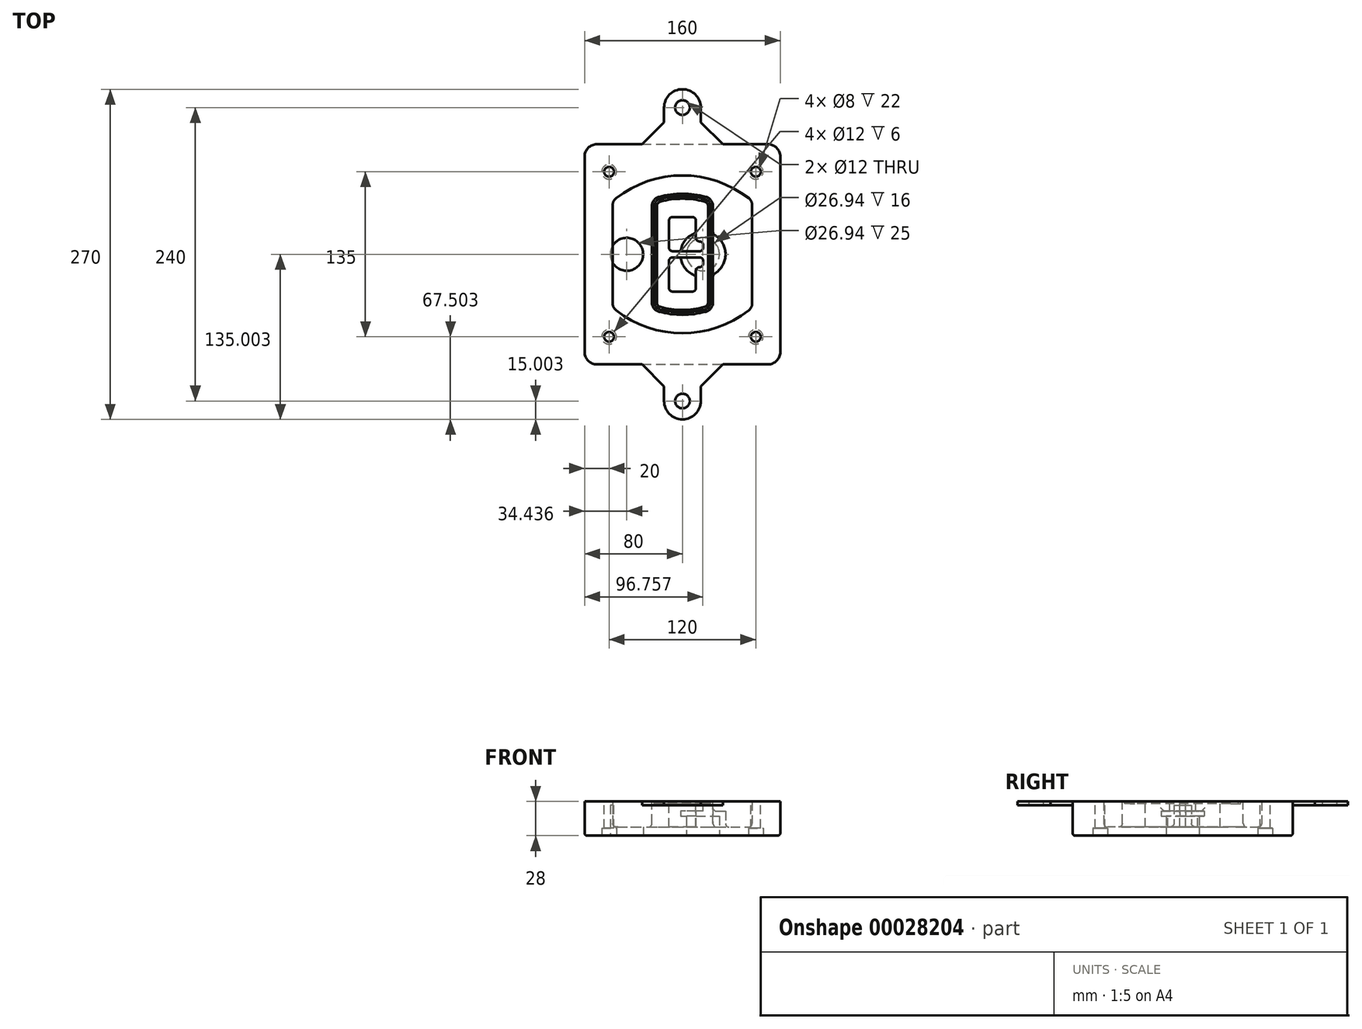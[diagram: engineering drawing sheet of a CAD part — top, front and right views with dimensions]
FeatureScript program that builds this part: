
annotation { "Feature Type Name" : "Feature", "Feature Type Description" : "" }
export const myFeature = defineFeature(function(context is Context, id is Id, definition is map)
    precondition{}
    {
        {
            var Q0;
            Q0=qCreatedBy(makeId("Top.planeOp"),FACE);
            var sketch = newSketch(context, id + "F0", { "sketchPlane" : qUnion([Q0])});
            skPoint(sketch, "E0.rect.middle", {"position": v(0, 0) * mm});
            skLineSegment(sketch, "E1.bottom", {"start": v(24.05, 28.38) * mm, "end": v(164.05, 28.38) * mm});
            skLineSegment(sketch, "E1.top", {"start": v(24.05, 208.38) * mm, "end": v(164.05, 208.38) * mm});
            skLineSegment(sketch, "E1.left", {"start": v(14.05, 38.38) * mm, "end": v(14.05, 198.38) * mm});
            skLineSegment(sketch, "E1.right", {"start": v(174.05, 38.38) * mm, "end": v(174.05, 198.38) * mm});
            skLineSegment(sketch, "E2", {"start": v(14.05, 208.38) * mm, "end": v(174.05, 28.38) * mm, "construction": true});
            skLineSegment(sketch, "E3", {"start": v(174.05, 208.38) * mm, "end": v(14.05, 28.38) * mm, "construction": true});
            skCircle(sketch, "E4", {"center": v(34.05, 185.88) * mm, "radius": 4 * mm});
            skCircle(sketch, "E5", {"center": v(154.05, 185.88) * mm, "radius": 4 * mm});
            skCircle(sketch, "E6", {"center": v(154.05, 50.88) * mm, "radius": 4 * mm});
            skCircle(sketch, "E7", {"center": v(34.05, 50.88) * mm, "radius": 4 * mm});
            skLineSegment(sketch, "E8", {"start": v(34.05, 185.88) * mm, "end": v(154.05, 185.88) * mm, "construction": true});
            skLineSegment(sketch, "E9", {"start": v(154.05, 185.88) * mm, "end": v(154.05, 50.88) * mm, "construction": true});
            skLineSegment(sketch, "E10", {"start": v(154.05, 50.88) * mm, "end": v(34.05, 50.88) * mm, "construction": true});
            skLineSegment(sketch, "E11", {"start": v(34.05, 50.88) * mm, "end": v(34.05, 185.88) * mm, "construction": true});
            skLineSegment(sketch, "E12", {"start": v(34.05, 158.68) * mm, "end": v(34.05, 78.09) * mm});
            skLineSegment(sketch, "E13", {"start": v(154.05, 158.68) * mm, "end": v(154.05, 78.09) * mm});
            skArc(sketch, "E14", {"start": v(150.2, 166.56) * mm, "mid": v(94.05, 185.88) * mm, "end": v(37.9, 166.56) * mm});
            skArc(sketch, "E15", {"start": v(37.9, 70.2) * mm, "mid": v(94.05, 50.88) * mm, "end": v(150.2, 70.2) * mm});
            skLineSegment(sketch, "E16", {"start": v(34.05, 118.38) * mm, "end": v(154.05, 118.38) * mm, "construction": true});
            skPoint(sketch, "E17.visualSharp", {"position": v(34.05, 73.38) * mm});
            skArc(sketch, "E17.filletArc", {"start": v(34.05, 78.09) * mm, "mid": v(35.06, 73.7) * mm, "end": v(37.9, 70.2) * mm});
            skPoint(sketch, "E18.visualSharp", {"position": v(34.05, 163.38) * mm});
            skArc(sketch, "E18.filletArc", {"start": v(37.9, 166.56) * mm, "mid": v(35.06, 163.06) * mm, "end": v(34.05, 158.68) * mm});
            skPoint(sketch, "E19.visualSharp", {"position": v(154.05, 163.38) * mm});
            skArc(sketch, "E19.filletArc", {"start": v(154.05, 158.68) * mm, "mid": v(153.04, 163.06) * mm, "end": v(150.2, 166.56) * mm});
            skPoint(sketch, "E20.visualSharp", {"position": v(154.05, 73.38) * mm});
            skArc(sketch, "E20.filletArc", {"start": v(150.2, 70.2) * mm, "mid": v(153.04, 73.7) * mm, "end": v(154.05, 78.09) * mm});
            skPoint(sketch, "E21.visualSharp", {"position": v(14.05, 208.38) * mm});
            skArc(sketch, "E21.filletArc", {"start": v(24.05, 208.38) * mm, "mid": v(16.98, 205.45) * mm, "end": v(14.05, 198.38) * mm});
            skPoint(sketch, "E22.visualSharp", {"position": v(174.05, 208.38) * mm});
            skArc(sketch, "E22.filletArc", {"start": v(174.05, 198.38) * mm, "mid": v(171.12, 205.45) * mm, "end": v(164.05, 208.38) * mm});
            skPoint(sketch, "E23.visualSharp", {"position": v(174.05, 28.38) * mm});
            skArc(sketch, "E23.filletArc", {"start": v(164.05, 28.38) * mm, "mid": v(171.12, 31.31) * mm, "end": v(174.05, 38.38) * mm});
            skPoint(sketch, "E24.visualSharp", {"position": v(14.05, 28.38) * mm});
            skArc(sketch, "E24.filletArc", {"start": v(14.05, 38.38) * mm, "mid": v(16.98, 31.31) * mm, "end": v(24.05, 28.38) * mm});
            skArc(sketch, "E25.0", {"start": v(151.05, 158.68) * mm, "mid": v(150.34, 161.75) * mm, "end": v(148.36, 164.2) * mm});
            skLineSegment(sketch, "E25.1", {"start": v(151.05, 158.68) * mm, "end": v(151.05, 78.09) * mm});
            skArc(sketch, "E25.2", {"start": v(148.36, 72.57) * mm, "mid": v(150.34, 75.02) * mm, "end": v(151.05, 78.09) * mm});
            skArc(sketch, "E25.3", {"start": v(39.74, 72.57) * mm, "mid": v(94.05, 53.88) * mm, "end": v(148.36, 72.57) * mm});
            skArc(sketch, "E25.4", {"start": v(37.05, 78.09) * mm, "mid": v(37.76, 75.02) * mm, "end": v(39.74, 72.57) * mm});
            skArc(sketch, "E25.5", {"start": v(148.36, 164.2) * mm, "mid": v(94.05, 182.88) * mm, "end": v(39.74, 164.2) * mm});
            skLineSegment(sketch, "E25.6", {"start": v(37.05, 158.68) * mm, "end": v(37.05, 78.09) * mm});
            skArc(sketch, "E25.7", {"start": v(39.74, 164.2) * mm, "mid": v(37.76, 161.75) * mm, "end": v(37.05, 158.68) * mm});
            skArc(sketch, "E26.0", {"start": v(35.43, 169.71) * mm, "mid": v(31.47, 164.82) * mm, "end": v(30.05, 158.68) * mm});
            skArc(sketch, "E26.1", {"start": v(152.67, 169.71) * mm, "mid": v(94.05, 189.88) * mm, "end": v(35.43, 169.71) * mm});
            skArc(sketch, "E26.2", {"start": v(158.05, 158.68) * mm, "mid": v(156.63, 164.82) * mm, "end": v(152.67, 169.71) * mm});
            skLineSegment(sketch, "E26.3", {"start": v(158.05, 158.68) * mm, "end": v(158.05, 78.09) * mm});
            skArc(sketch, "E26.4", {"start": v(152.67, 67.05) * mm, "mid": v(156.63, 71.95) * mm, "end": v(158.05, 78.09) * mm});
            skLineSegment(sketch, "E26.5", {"start": v(30.05, 158.68) * mm, "end": v(30.05, 78.09) * mm});
            skArc(sketch, "E26.6", {"start": v(35.43, 67.05) * mm, "mid": v(94.05, 46.88) * mm, "end": v(152.67, 67.05) * mm});
            skArc(sketch, "E26.7", {"start": v(30.05, 78.09) * mm, "mid": v(31.47, 71.95) * mm, "end": v(35.43, 67.05) * mm});
            skSolve(sketch);
        }
        {
            var Q0;
            Q0=makeQuery(id+"F0.imprint","IMPRINT",FACE,{"disambiguationData":[TD([[makeQuery(id+"F0.imprint","IMPRINT",EDGE,{"derivedFrom":sQuery(id+"F0.wireOp",EDGE,"E1.bottom")}),1.0]])]});
            var Q1;
            Q1=makeQuery(id+"F0.imprint","IMPRINT",FACE,{"disambiguationData":[TD([[makeQuery(id+"F0.imprint","IMPRINT",EDGE,{"derivedFrom":sQuery(id+"F0.wireOp",EDGE,"E12")}),1.0]])]});
            var Q2;
            Q2=makeQuery(id+"F0.imprint","IMPRINT",FACE,{"disambiguationData":[TD([[makeQuery(id+"F0.imprint","IMPRINT",EDGE,{"derivedFrom":sQuery(id+"F0.wireOp",EDGE,"E25.0")}),1.0]])]});
            var Q3;
            Q3=makeQuery(id+"F0.imprint","IMPRINT",FACE,{"disambiguationData":[TD([[makeQuery(id+"F0.imprint","IMPRINT",EDGE,{"derivedFrom":sQuery(id+"F0.wireOp",EDGE,"E12")}),-1.0]])]});
            extrude(context, id + "F1", {"entities" : qUnion([Q0, Q1, Q2, Q3]), "oppositeDirection" : true, "depth" : 25 * mm});
        }
        {
            var Q0;
            Q0=makeQuery(id+"F0.imprint","IMPRINT",FACE,{"disambiguationData":[TD([[makeQuery(id+"F0.imprint","IMPRINT",EDGE,{"derivedFrom":sQuery(id+"F0.wireOp",EDGE,"E12")}),1.0]])]});
            extrude(context, id + "F2", {"entities" : qUnion([Q0]), "operationType" : NewBodyOperationType.ADD, "depth" : 3 * mm});
        }
        {
            var Q0;
            Q0=makeQuery(id+"F0.imprint","IMPRINT",FACE,{"disambiguationData":[TD([[makeQuery(id+"F0.imprint","IMPRINT",EDGE,{"derivedFrom":sQuery(id+"F0.wireOp",EDGE,"E25.0")}),1.0]])]});
            extrude(context, id + "F3", {"entities" : qUnion([Q0]), "operationType" : NewBodyOperationType.REMOVE, "oppositeDirection" : true, "depth" : 18 * mm});
        }
        {
            var Q0;
            Q0=makeQuery(id+"F2.opExtrude","CAP_FACE",FACE,{"disambiguationData":[OSD([sQuery(id+"F0.wireOp",EDGE,"E12"),sQuery(id+"F0.wireOp",EDGE,"E13"),sQuery(id+"F0.wireOp",EDGE,"E14"),sQuery(id+"F0.wireOp",EDGE,"E15"),sQuery(id+"F0.wireOp",EDGE,"E17.filletArc"),sQuery(id+"F0.wireOp",EDGE,"E18.filletArc"),sQuery(id+"F0.wireOp",EDGE,"E19.filletArc"),sQuery(id+"F0.wireOp",EDGE,"E20.filletArc"),sQuery(id+"F0.wireOp",EDGE,"E25.0"),sQuery(id+"F0.wireOp",EDGE,"E25.1"),sQuery(id+"F0.wireOp",EDGE,"E25.2"),sQuery(id+"F0.wireOp",EDGE,"E25.3"),sQuery(id+"F0.wireOp",EDGE,"E25.4"),sQuery(id+"F0.wireOp",EDGE,"E25.5"),sQuery(id+"F0.wireOp",EDGE,"E25.6"),sQuery(id+"F0.wireOp",EDGE,"E25.7")])],"isStart":false});
            var sketch = newSketch(context, id + "F4", { "sketchPlane" : qUnion([Q0])});
            skArc(sketch, "E27.0", {"start": v(74.97, 71.41) * mm, "mid": v(94.05, 68.88) * mm, "end": v(113.13, 71.41) * mm});
            skArc(sketch, "E28.0", {"start": v(113.13, 165.35) * mm, "mid": v(94.05, 167.88) * mm, "end": v(74.97, 165.35) * mm});
            skLineSegment(sketch, "E29", {"start": v(69.05, 157.63) * mm, "end": v(69.05, 79.14) * mm});
            skLineSegment(sketch, "E30", {"start": v(119.05, 157.63) * mm, "end": v(119.05, 79.14) * mm});
            skLineSegment(sketch, "E31", {"start": v(69.05, 163.48) * mm, "end": v(119.05, 163.48) * mm, "construction": true});
            skLineSegment(sketch, "E32", {"start": v(69.05, 73.28) * mm, "end": v(119.05, 73.28) * mm, "construction": true});
            skPoint(sketch, "E33.visualSharp", {"position": v(69.05, 163.48) * mm});
            skArc(sketch, "E33.filletArc", {"start": v(74.97, 165.35) * mm, "mid": v(70.7, 162.5) * mm, "end": v(69.05, 157.63) * mm});
            skPoint(sketch, "E34.visualSharp", {"position": v(119.05, 163.48) * mm});
            skArc(sketch, "E34.filletArc", {"start": v(119.05, 157.63) * mm, "mid": v(117.4, 162.5) * mm, "end": v(113.13, 165.35) * mm});
            skPoint(sketch, "E35.visualSharp", {"position": v(119.05, 73.28) * mm});
            skArc(sketch, "E35.filletArc", {"start": v(113.13, 71.41) * mm, "mid": v(117.4, 74.27) * mm, "end": v(119.05, 79.14) * mm});
            skPoint(sketch, "E36.visualSharp", {"position": v(69.05, 73.28) * mm});
            skArc(sketch, "E36.filletArc", {"start": v(69.05, 79.14) * mm, "mid": v(70.7, 74.27) * mm, "end": v(74.97, 71.41) * mm});
            skArc(sketch, "E37.0", {"start": v(148.36, 164.2) * mm, "mid": v(94.05, 182.88) * mm, "end": v(39.74, 164.2) * mm});
            skArc(sketch, "E37.1", {"start": v(39.74, 164.2) * mm, "mid": v(37.76, 161.75) * mm, "end": v(37.05, 158.68) * mm});
            skLineSegment(sketch, "E37.2", {"start": v(37.05, 158.68) * mm, "end": v(37.05, 78.09) * mm});
            skArc(sketch, "E37.3", {"start": v(37.05, 78.09) * mm, "mid": v(37.76, 75.02) * mm, "end": v(39.74, 72.57) * mm});
            skArc(sketch, "E37.4", {"start": v(39.74, 72.57) * mm, "mid": v(94.05, 53.88) * mm, "end": v(148.36, 72.57) * mm});
            skArc(sketch, "E37.5", {"start": v(148.36, 72.57) * mm, "mid": v(150.34, 75.02) * mm, "end": v(151.05, 78.09) * mm});
            skLineSegment(sketch, "E37.6", {"start": v(151.05, 158.68) * mm, "end": v(151.05, 78.09) * mm});
            skArc(sketch, "E37.7", {"start": v(151.05, 158.68) * mm, "mid": v(150.34, 161.75) * mm, "end": v(148.36, 164.2) * mm});
            skLineSegment(sketch, "E38.0", {"start": v(117.05, 157.63) * mm, "end": v(117.05, 79.14) * mm});
            skArc(sketch, "E38.1", {"start": v(112.61, 73.34) * mm, "mid": v(115.81, 75.49) * mm, "end": v(117.05, 79.14) * mm});
            skArc(sketch, "E38.2", {"start": v(75.49, 73.34) * mm, "mid": v(94.05, 70.88) * mm, "end": v(112.61, 73.34) * mm});
            skArc(sketch, "E38.3", {"start": v(71.05, 79.14) * mm, "mid": v(72.29, 75.49) * mm, "end": v(75.49, 73.34) * mm});
            skLineSegment(sketch, "E38.4", {"start": v(71.05, 157.63) * mm, "end": v(71.05, 79.14) * mm});
            skArc(sketch, "E38.5", {"start": v(117.05, 157.63) * mm, "mid": v(115.81, 161.28) * mm, "end": v(112.61, 163.42) * mm});
            skArc(sketch, "E38.6", {"start": v(75.49, 163.42) * mm, "mid": v(72.29, 161.28) * mm, "end": v(71.05, 157.63) * mm});
            skArc(sketch, "E38.7", {"start": v(112.61, 163.42) * mm, "mid": v(94.05, 165.88) * mm, "end": v(75.49, 163.42) * mm});
            skArc(sketch, "E39.0", {"start": v(115.05, 157.63) * mm, "mid": v(114.23, 160.06) * mm, "end": v(112.1, 161.5) * mm});
            skLineSegment(sketch, "E39.1", {"start": v(115.05, 157.63) * mm, "end": v(115.05, 79.14) * mm});
            skArc(sketch, "E39.2", {"start": v(112.1, 75.27) * mm, "mid": v(114.23, 76.7) * mm, "end": v(115.05, 79.14) * mm});
            skArc(sketch, "E39.3", {"start": v(76, 75.27) * mm, "mid": v(94.05, 72.88) * mm, "end": v(112.1, 75.27) * mm});
            skArc(sketch, "E39.4", {"start": v(73.05, 79.14) * mm, "mid": v(73.87, 76.7) * mm, "end": v(76, 75.27) * mm});
            skArc(sketch, "E39.5", {"start": v(112.1, 161.5) * mm, "mid": v(94.05, 163.88) * mm, "end": v(76, 161.5) * mm});
            skLineSegment(sketch, "E39.6", {"start": v(73.05, 157.63) * mm, "end": v(73.05, 79.14) * mm});
            skArc(sketch, "E39.7", {"start": v(76, 161.5) * mm, "mid": v(73.87, 160.06) * mm, "end": v(73.05, 157.63) * mm});
            skLineSegment(sketch, "E40", {"start": v(69.05, 118.38) * mm, "end": v(119.05, 118.38) * mm, "construction": true});
            skLineSegment(sketch, "E41", {"start": v(83.05, 123.88) * mm, "end": v(83.05, 145.88) * mm});
            skLineSegment(sketch, "E42", {"start": v(86.05, 148.88) * mm, "end": v(102.05, 148.88) * mm});
            skLineSegment(sketch, "E43", {"start": v(105.05, 145.88) * mm, "end": v(105.05, 131.88) * mm});
            skLineSegment(sketch, "E44", {"start": v(108.05, 128.88) * mm, "end": v(108.05, 128.88) * mm});
            skLineSegment(sketch, "E45", {"start": v(111.05, 125.88) * mm, "end": v(111.05, 123.88) * mm});
            skLineSegment(sketch, "E46", {"start": v(108.05, 120.88) * mm, "end": v(86.05, 120.88) * mm});
            skPoint(sketch, "E47.visualSharp", {"position": v(83.05, 148.88) * mm});
            skArc(sketch, "E47.filletArc", {"start": v(86.05, 148.88) * mm, "mid": v(83.93, 148) * mm, "end": v(83.05, 145.88) * mm});
            skPoint(sketch, "E48.visualSharp", {"position": v(105.05, 148.88) * mm});
            skArc(sketch, "E48.filletArc", {"start": v(105.05, 145.88) * mm, "mid": v(104.17, 148) * mm, "end": v(102.05, 148.88) * mm});
            skPoint(sketch, "E49.visualSharp", {"position": v(105.05, 128.88) * mm});
            skArc(sketch, "E49.filletArc", {"start": v(105.05, 131.88) * mm, "mid": v(105.93, 129.76) * mm, "end": v(108.05, 128.88) * mm});
            skPoint(sketch, "E50.visualSharp", {"position": v(111.05, 128.88) * mm});
            skArc(sketch, "E50.filletArc", {"start": v(111.05, 125.88) * mm, "mid": v(110.17, 128) * mm, "end": v(108.05, 128.88) * mm});
            skPoint(sketch, "E51.visualSharp", {"position": v(111.05, 120.88) * mm});
            skArc(sketch, "E51.filletArc", {"start": v(108.05, 120.88) * mm, "mid": v(110.17, 121.76) * mm, "end": v(111.05, 123.88) * mm});
            skPoint(sketch, "E52.visualSharp", {"position": v(83.05, 120.88) * mm});
            skArc(sketch, "E52.filletArc", {"start": v(83.05, 123.88) * mm, "mid": v(83.93, 121.76) * mm, "end": v(86.05, 120.88) * mm});
            skLineSegment(sketch, "E53.0.MirrorCS", {"start": v(108.05, 115.88) * mm, "end": v(86.05, 115.88) * mm});
            skArc(sketch, "E54.0.MirrorCS", {"start": v(83.05, 112.88) * mm, "mid": v(83.93, 115) * mm, "end": v(86.05, 115.88) * mm});
            skLineSegment(sketch, "E55.0.MirrorCS", {"start": v(83.05, 112.88) * mm, "end": v(83.05, 90.88) * mm});
            skArc(sketch, "E56.0.MirrorCS", {"start": v(86.05, 87.88) * mm, "mid": v(83.93, 88.76) * mm, "end": v(83.05, 90.88) * mm});
            skLineSegment(sketch, "E57.0.MirrorCS", {"start": v(86.05, 87.88) * mm, "end": v(102.05, 87.88) * mm});
            skArc(sketch, "E58.0.MirrorCS", {"start": v(105.05, 90.88) * mm, "mid": v(104.17, 88.76) * mm, "end": v(102.05, 87.88) * mm});
            skLineSegment(sketch, "E59.0.MirrorCS", {"start": v(105.05, 90.88) * mm, "end": v(105.05, 104.88) * mm});
            skArc(sketch, "E60.0.MirrorCS", {"start": v(105.05, 104.88) * mm, "mid": v(105.93, 107) * mm, "end": v(108.05, 107.88) * mm});
            skArc(sketch, "E61.0.MirrorCS", {"start": v(111.05, 110.88) * mm, "mid": v(110.17, 108.76) * mm, "end": v(108.05, 107.88) * mm});
            skLineSegment(sketch, "E62.0.MirrorCS", {"start": v(111.05, 110.88) * mm, "end": v(111.05, 112.88) * mm});
            skArc(sketch, "E63.0.MirrorCS", {"start": v(108.05, 115.88) * mm, "mid": v(110.17, 115) * mm, "end": v(111.05, 112.88) * mm});
            skSolve(sketch);
        }
        {
            var Q0;
            Q0=makeQuery(id+"F4.imprint","IMPRINT",FACE,{"disambiguationData":[TD([[makeQuery(id+"F4.imprint","IMPRINT",EDGE,{"derivedFrom":sQuery(id+"F4.wireOp",EDGE,"E27.0")}),1.0]])]});
            var Q1;
            Q1=makeQuery(id+"F4.imprint","IMPRINT",FACE,{"disambiguationData":[TD([[makeQuery(id+"F4.imprint","IMPRINT",EDGE,{"derivedFrom":sQuery(id+"F4.wireOp",EDGE,"E38.0")}),-1.0]])]});
            var Q2;
            Q2=makeQuery(id+"F4.imprint","IMPRINT",FACE,{"disambiguationData":[TD([[makeQuery(id+"F4.imprint","IMPRINT",EDGE,{"derivedFrom":sQuery(id+"F4.wireOp",EDGE,"E39.0")}),1.0]])]});
            extrude(context, id + "F5", {"entities" : qUnion([Q0, Q1, Q2]), "operationType" : NewBodyOperationType.ADD, "endBound" : BoundingType.UP_TO_NEXT, "oppositeDirection" : true, "depth" : 25 * mm});
        }
        {
            var Q0;
            Q0=makeQuery(id+"F4.imprint","IMPRINT",FACE,{"disambiguationData":[TD([[makeQuery(id+"F4.imprint","IMPRINT",EDGE,{"derivedFrom":sQuery(id+"F4.wireOp",EDGE,"E38.0")}),-1.0]])]});
            extrude(context, id + "F6", {"entities" : qUnion([Q0]), "operationType" : NewBodyOperationType.REMOVE, "oppositeDirection" : true, "depth" : 2 * mm});
        }
        {
            var Q0;
            Q0=makeQuery(id+"F1.opExtrude","CAP_FACE",FACE,{"disambiguationData":[OSD([sQuery(id+"F0.wireOp",EDGE,"E1.bottom"),sQuery(id+"F0.wireOp",EDGE,"E1.top"),sQuery(id+"F0.wireOp",EDGE,"E1.left"),sQuery(id+"F0.wireOp",EDGE,"E1.right"),sQuery(id+"F0.wireOp",EDGE,"E4"),sQuery(id+"F0.wireOp",EDGE,"E5"),sQuery(id+"F0.wireOp",EDGE,"E6"),sQuery(id+"F0.wireOp",EDGE,"E7"),sQuery(id+"F0.wireOp",EDGE,"E21.filletArc"),sQuery(id+"F0.wireOp",EDGE,"E22.filletArc"),sQuery(id+"F0.wireOp",EDGE,"E23.filletArc"),sQuery(id+"F0.wireOp",EDGE,"E24.filletArc")])],"isStart":false});
            var sketch = newSketch(context, id + "F7", { "sketchPlane" : qUnion([Q0])});
            skCircle(sketch, "E64", {"center": v(110.8, -118.38) * mm, "radius": 13.47 * mm});
            skCircle(sketch, "E65", {"center": v(48.49, -118.38) * mm, "radius": 13.47 * mm});
            skLineSegment(sketch, "E66", {"start": v(174.05, -118.38) * mm, "end": v(14.05, -118.38) * mm});
            skCircle(sketch, "E67", {"center": v(110.8, -118.38) * mm, "radius": 18.47 * mm});
            skCircle(sketch, "E68", {"center": v(154.05, -185.88) * mm, "radius": 6 * mm});
            skCircle(sketch, "E69", {"center": v(34.05, -185.88) * mm, "radius": 6 * mm});
            skCircle(sketch, "E70", {"center": v(34.05, -50.88) * mm, "radius": 6 * mm});
            skCircle(sketch, "E71", {"center": v(154.05, -50.88) * mm, "radius": 6 * mm});
            skSolve(sketch);
        }
        {
            var Q0;
            {var subQ1=sQuery(id+"F7.wireOp",EDGE,"E66");var subQ4=sQuery(id+"F7.wireOp",EDGE,"E64");var subQ6=makeQuery(id+"F7.imprint","INTERSECT",VERTEX,{"disambiguationData":[OD(0.0)],"derivedFrom":[subQ4,subQ1]});Q0=makeQuery(id+"F7.imprint","IMPRINT",FACE,{"disambiguationData":[TD([[makeQuery(id+"F7.imprint","IMPRINT",EDGE,{"disambiguationData":[TD([[subQ6,-1.0]])],"derivedFrom":subQ4}),-1.0]])]});}
            var Q1;
            {var subQ0=sQuery(id+"F7.wireOp",EDGE,"E66");var subQ1=sQuery(id+"F7.wireOp",EDGE,"E64");var subQ3=makeQuery(id+"F7.imprint","INTERSECT",VERTEX,{"disambiguationData":[OD(0.0)],"derivedFrom":[subQ1,subQ0]});Q1=makeQuery(id+"F7.imprint","IMPRINT",FACE,{"disambiguationData":[TD([[makeQuery(id+"F7.imprint","IMPRINT",EDGE,{"disambiguationData":[TD([[subQ3,-1.0]])],"derivedFrom":subQ1}),1.0]])]});}
            var Q2;
            {var subQ0=sQuery(id+"F7.wireOp",EDGE,"E66");var subQ1=sQuery(id+"F7.wireOp",EDGE,"E64");var subQ3=makeQuery(id+"F7.imprint","INTERSECT",VERTEX,{"disambiguationData":[OD(0.0)],"derivedFrom":[subQ1,subQ0]});Q2=makeQuery(id+"F7.imprint","IMPRINT",FACE,{"disambiguationData":[TD([[makeQuery(id+"F7.imprint","IMPRINT",EDGE,{"disambiguationData":[TD([[subQ3,1.0]])],"derivedFrom":subQ1}),1.0]])]});}
            var Q3;
            {var subQ1=sQuery(id+"F7.wireOp",EDGE,"E66");var subQ4=sQuery(id+"F7.wireOp",EDGE,"E64");var subQ6=makeQuery(id+"F7.imprint","INTERSECT",VERTEX,{"disambiguationData":[OD(0.0)],"derivedFrom":[subQ4,subQ1]});Q3=makeQuery(id+"F7.imprint","IMPRINT",FACE,{"disambiguationData":[TD([[makeQuery(id+"F7.imprint","IMPRINT",EDGE,{"disambiguationData":[TD([[subQ6,1.0]])],"derivedFrom":subQ4}),-1.0]])]});}
            extrude(context, id + "F8", {"entities" : qUnion([Q0, Q1, Q2, Q3]), "operationType" : NewBodyOperationType.ADD, "oppositeDirection" : true, "depth" : 20 * mm});
        }
        {
            var Q0;
            {var subQ0=sQuery(id+"F7.wireOp",EDGE,"E66");var subQ1=sQuery(id+"F7.wireOp",EDGE,"E64");var subQ3=makeQuery(id+"F7.imprint","INTERSECT",VERTEX,{"disambiguationData":[OD(0.0)],"derivedFrom":[subQ1,subQ0]});Q0=makeQuery(id+"F7.imprint","IMPRINT",FACE,{"disambiguationData":[TD([[makeQuery(id+"F7.imprint","IMPRINT",EDGE,{"disambiguationData":[TD([[subQ3,-1.0]])],"derivedFrom":subQ1}),1.0]])]});}
            var Q1;
            {var subQ0=sQuery(id+"F7.wireOp",EDGE,"E66");var subQ1=sQuery(id+"F7.wireOp",EDGE,"E64");var subQ3=makeQuery(id+"F7.imprint","INTERSECT",VERTEX,{"disambiguationData":[OD(0.0)],"derivedFrom":[subQ1,subQ0]});Q1=makeQuery(id+"F7.imprint","IMPRINT",FACE,{"disambiguationData":[TD([[makeQuery(id+"F7.imprint","IMPRINT",EDGE,{"disambiguationData":[TD([[subQ3,1.0]])],"derivedFrom":subQ1}),1.0]])]});}
            extrude(context, id + "F9", {"entities" : qUnion([Q0, Q1]), "operationType" : NewBodyOperationType.REMOVE, "oppositeDirection" : true, "depth" : 16 * mm});
        }
        {
            var Q0;
            {var subQ0=sQuery(id+"F7.wireOp",EDGE,"E66");var subQ1=sQuery(id+"F7.wireOp",EDGE,"E65");var subQ3=makeQuery(id+"F7.imprint","INTERSECT",VERTEX,{"disambiguationData":[OD(0.0)],"derivedFrom":[subQ1,subQ0]});Q0=makeQuery(id+"F7.imprint","IMPRINT",FACE,{"disambiguationData":[TD([[makeQuery(id+"F7.imprint","IMPRINT",EDGE,{"disambiguationData":[TD([[subQ3,-1.0]])],"derivedFrom":subQ1}),1.0]])]});}
            var Q1;
            {var subQ0=sQuery(id+"F7.wireOp",EDGE,"E66");var subQ1=sQuery(id+"F7.wireOp",EDGE,"E65");var subQ3=makeQuery(id+"F7.imprint","INTERSECT",VERTEX,{"disambiguationData":[OD(0.0)],"derivedFrom":[subQ1,subQ0]});Q1=makeQuery(id+"F7.imprint","IMPRINT",FACE,{"disambiguationData":[TD([[makeQuery(id+"F7.imprint","IMPRINT",EDGE,{"disambiguationData":[TD([[subQ3,1.0]])],"derivedFrom":subQ1}),1.0]])]});}
            extrude(context, id + "F10", {"entities" : qUnion([Q0, Q1]), "operationType" : NewBodyOperationType.REMOVE, "oppositeDirection" : true, "depth" : 25 * mm});
        }
        {
            var Q0;
            Q0=makeQuery(id+"F7.imprint","IMPRINT",FACE,{"disambiguationData":[TD([[makeQuery(id+"F7.imprint","IMPRINT",EDGE,{"derivedFrom":sQuery(id+"F7.wireOp",EDGE,"E68")}),1.0]])]});
            var Q1;
            Q1=makeQuery(id+"F7.imprint","IMPRINT",FACE,{"disambiguationData":[TD([[makeQuery(id+"F7.imprint","IMPRINT",EDGE,{"derivedFrom":makeQuery(id+"F1.opExtrude","CAP_EDGE",EDGE,{"disambiguationData":[OSD([sQuery(id+"F0.wireOp",EDGE,"E5")])],"isStart":false})}),-1.0]])]});
            var Q2;
            Q2=makeQuery(id+"F7.imprint","IMPRINT",FACE,{"disambiguationData":[TD([[makeQuery(id+"F7.imprint","IMPRINT",EDGE,{"derivedFrom":sQuery(id+"F7.wireOp",EDGE,"E69")}),1.0]])]});
            var Q3;
            Q3=makeQuery(id+"F7.imprint","IMPRINT",FACE,{"disambiguationData":[TD([[makeQuery(id+"F7.imprint","IMPRINT",EDGE,{"derivedFrom":makeQuery(id+"F1.opExtrude","CAP_EDGE",EDGE,{"disambiguationData":[OSD([sQuery(id+"F0.wireOp",EDGE,"E4")])],"isStart":false})}),-1.0]])]});
            var Q4;
            Q4=makeQuery(id+"F7.imprint","IMPRINT",FACE,{"disambiguationData":[TD([[makeQuery(id+"F7.imprint","IMPRINT",EDGE,{"derivedFrom":sQuery(id+"F7.wireOp",EDGE,"E70")}),1.0]])]});
            var Q5;
            Q5=makeQuery(id+"F7.imprint","IMPRINT",FACE,{"disambiguationData":[TD([[makeQuery(id+"F7.imprint","IMPRINT",EDGE,{"derivedFrom":makeQuery(id+"F1.opExtrude","CAP_EDGE",EDGE,{"disambiguationData":[OSD([sQuery(id+"F0.wireOp",EDGE,"E7")])],"isStart":false})}),-1.0]])]});
            var Q6;
            Q6=makeQuery(id+"F7.imprint","IMPRINT",FACE,{"disambiguationData":[TD([[makeQuery(id+"F7.imprint","IMPRINT",EDGE,{"derivedFrom":sQuery(id+"F7.wireOp",EDGE,"E71")}),1.0]])]});
            var Q7;
            Q7=makeQuery(id+"F7.imprint","IMPRINT",FACE,{"disambiguationData":[TD([[makeQuery(id+"F7.imprint","IMPRINT",EDGE,{"derivedFrom":makeQuery(id+"F1.opExtrude","CAP_EDGE",EDGE,{"disambiguationData":[OSD([sQuery(id+"F0.wireOp",EDGE,"E6")])],"isStart":false})}),-1.0]])]});
            extrude(context, id + "F11", {"entities" : qUnion([Q0, Q1, Q2, Q3, Q4, Q5, Q6, Q7]), "operationType" : NewBodyOperationType.REMOVE, "oppositeDirection" : true, "depth" : 6 * mm});
        }
        {
            var Q0;
            Q0=makeQuery(id+"F9.boolean.opBoolean","COPY",FACE,{"derivedFrom":makeQuery(id+"F9.opExtrude","CAP_FACE",FACE,{"disambiguationData":[OSD([sQuery(id+"F7.wireOp",EDGE,"E64")])],"isStart":false})});
            var sketch = newSketch(context, id + "F12", { "sketchPlane" : qUnion([Q0])});
            skArc(sketch, "E72.0", {"start": v(105.05, -100.83) * mm, "mid": v(96.62, -106.56) * mm, "end": v(92.5, -115.88) * mm});
            skArc(sketch, "E72.1", {"start": v(92.5, -120.88) * mm, "mid": v(96.62, -130.2) * mm, "end": v(105.05, -135.93) * mm});
            skLineSegment(sketch, "E73", {"start": v(92.5, -120.88) * mm, "end": v(108.05, -120.88) * mm});
            skLineSegment(sketch, "E74.0", {"start": v(108.05, -115.88) * mm, "end": v(92.5, -115.88) * mm});
            skArc(sketch, "E74.1", {"start": v(108.05, -115.88) * mm, "mid": v(110.17, -115) * mm, "end": v(111.05, -112.88) * mm});
            skLineSegment(sketch, "E74.2", {"start": v(111.05, -110.88) * mm, "end": v(111.05, -112.88) * mm});
            skArc(sketch, "E74.3", {"start": v(111.05, -110.88) * mm, "mid": v(110.17, -108.76) * mm, "end": v(108.05, -107.88) * mm});
            skArc(sketch, "E74.4", {"start": v(105.05, -104.88) * mm, "mid": v(105.93, -107) * mm, "end": v(108.05, -107.88) * mm});
            skLineSegment(sketch, "E74.5", {"start": v(105.05, -100.83) * mm, "end": v(105.05, -104.88) * mm});
            skLineSegment(sketch, "E74.7", {"start": v(108.05, -120.88) * mm, "end": v(92.5, -120.88) * mm});
            skArc(sketch, "E74.8", {"start": v(108.05, -120.88) * mm, "mid": v(110.17, -121.76) * mm, "end": v(111.05, -123.88) * mm});
            skLineSegment(sketch, "E74.9", {"start": v(111.05, -125.88) * mm, "end": v(111.05, -123.88) * mm});
            skArc(sketch, "E74.10", {"start": v(111.05, -125.88) * mm, "mid": v(110.17, -128) * mm, "end": v(108.05, -128.88) * mm});
            skArc(sketch, "E74.11", {"start": v(105.05, -131.88) * mm, "mid": v(105.93, -129.76) * mm, "end": v(108.05, -128.88) * mm});
            skLineSegment(sketch, "E74.12", {"start": v(105.05, -135.93) * mm, "end": v(105.05, -131.88) * mm});
            skPoint(sketch, "E75.orphan", {"position": v(105.05, -145.88) * mm});
            skPoint(sketch, "E76.orphan", {"position": v(86.05, -120.88) * mm});
            skPoint(sketch, "E77.orphan", {"position": v(86.05, -115.88) * mm});
            skPoint(sketch, "E78.orphan", {"position": v(105.05, -90.88) * mm});
            skSolve(sketch);
        }
        {
            var Q0;
            {var subQ7=sQuery(id+"F12.wireOp",EDGE,"E72.0");var subQ14=sQuery(id+"F12.wireOp",EDGE,"E72.1");var subQ16=sQuery(id+"F12.wireOp",EDGE,"E74.1");var subQ18=sQuery(id+"F12.wireOp",EDGE,"E74.8");Q0=qUnion([makeQuery(id+"F12.imprint","IMPRINT",FACE,{"disambiguationData":[TD([[makeQuery(id+"F12.imprint","IMPRINT",EDGE,{"derivedFrom":subQ7}),1.0]])]}),makeQuery(id+"F12.imprint","IMPRINT",FACE,{"disambiguationData":[TD([[makeQuery(id+"F12.imprint","IMPRINT",EDGE,{"derivedFrom":subQ14}),1.0]])]}),makeQuery(id+"F12.imprint","IMPRINT",FACE,{"disambiguationData":[TD([[makeQuery(id+"F12.imprint","IMPRINT",EDGE,{"derivedFrom":subQ16}),1.0]])]}),makeQuery(id+"F12.imprint","IMPRINT",FACE,{"disambiguationData":[TD([[makeQuery(id+"F12.imprint","IMPRINT",EDGE,{"derivedFrom":subQ18}),-1.0]])]})]);}
            var Q1;
            Q1=makeQuery(id+"F5.boolean.opBoolean","SPLIT",FACE,{"disambiguationData":[TD([makeQuery(id+"F5.opExtrude","SWEPT_FACE",FACE,{"disambiguationData":[OSD([sQuery(id+"F4.wireOp",EDGE,"E41")])]})])],"derivedFrom":makeQuery(id+"F3.boolean.opBoolean","COPY",FACE,{"derivedFrom":makeQuery(id+"F3.opExtrude","CAP_FACE",FACE,{"disambiguationData":[OSD([sQuery(id+"F0.wireOp",EDGE,"E25.0"),sQuery(id+"F0.wireOp",EDGE,"E25.1"),sQuery(id+"F0.wireOp",EDGE,"E25.2"),sQuery(id+"F0.wireOp",EDGE,"E25.3"),sQuery(id+"F0.wireOp",EDGE,"E25.4"),sQuery(id+"F0.wireOp",EDGE,"E25.5"),sQuery(id+"F0.wireOp",EDGE,"E25.6"),sQuery(id+"F0.wireOp",EDGE,"E25.7")])],"isStart":false})})});
            extrude(context, id + "F13", {"entities" : qUnion([Q0]), "operationType" : NewBodyOperationType.REMOVE, "endBound" : BoundingType.UP_TO_SURFACE, "endBoundEntityFace" : qUnion([Q1]), "depth" : 25 * mm});
        }
        {
            var Q0;
            Q0=makeQuery(id+"F3.boolean.opBoolean","COPY",EDGE,{"derivedFrom":makeQuery(id+"F3.opExtrude","CAP_EDGE",EDGE,{"disambiguationData":[OSD([sQuery(id+"F0.wireOp",EDGE,"E25.6")])],"isStart":false})});
            var Q1;
            Q1=makeQuery(id+"F8.boolean.opBoolean","INTERSECT",EDGE,{"derivedFrom":[makeQuery(id+"F5.opExtrude","SWEPT_FACE",FACE,{"disambiguationData":[OSD([sQuery(id+"F4.wireOp",EDGE,"E30")])]}),makeQuery(id+"F8.opExtrude","CAP_FACE",FACE,{"disambiguationData":[OSD([sQuery(id+"F7.wireOp",EDGE,"E67")])],"isStart":false})]});
            var Q2;
            Q2=makeQuery(id+"F8.boolean.opBoolean","INTERSECT",EDGE,{"disambiguationData":[OD(1.0)],"derivedFrom":[makeQuery(id+"F5.opExtrude","SWEPT_FACE",FACE,{"disambiguationData":[OSD([sQuery(id+"F4.wireOp",EDGE,"E30")])]}),makeQuery(id+"F8.opExtrude","SWEPT_FACE",FACE,{"disambiguationData":[OSD([sQuery(id+"F7.wireOp",EDGE,"E67")])]})]});
            var Q3;
            {var subQ0=sQuery(id+"F4.wireOp",EDGE,"E30");Q3=makeQuery(id+"F8.boolean.opBoolean","SPLIT",EDGE,{"disambiguationData":[TD([makeQuery(id+"F5.opExtrude","SWEPT_FACE",FACE,{"disambiguationData":[OSD([sQuery(id+"F4.wireOp",EDGE,"E35.filletArc")])]})])],"derivedFrom":makeQuery(id+"F5.opExtrude","CAP_EDGE",EDGE,{"disambiguationData":[OSD([subQ0])],"isStart":false})});}
            var Q4;
            {var subQ0=sQuery(id+"F0.wireOp",EDGE,"E25.7");var subQ1=sQuery(id+"F0.wireOp",EDGE,"E25.1");var subQ2=sQuery(id+"F0.wireOp",EDGE,"E25.6");var subQ3=sQuery(id+"F0.wireOp",EDGE,"E25.5");var subQ4=sQuery(id+"F0.wireOp",EDGE,"E25.4");var subQ5=sQuery(id+"F0.wireOp",EDGE,"E25.0");var subQ6=sQuery(id+"F0.wireOp",EDGE,"E25.2");var subQ7=sQuery(id+"F0.wireOp",EDGE,"E25.3");Q4=makeQuery(id+"F8.boolean.opBoolean","INTERSECT",EDGE,{"derivedFrom":[makeQuery(id+"F5.boolean.opBoolean","SPLIT",FACE,{"disambiguationData":[TD([makeQuery(id+"F2.opExtrude","SWEPT_FACE",FACE,{"disambiguationData":[OSD([subQ5])]})])],"derivedFrom":makeQuery(id+"F3.boolean.opBoolean","COPY",FACE,{"derivedFrom":makeQuery(id+"F3.opExtrude","CAP_FACE",FACE,{"disambiguationData":[OSD([subQ5,subQ1,subQ6,subQ7,subQ4,subQ3,subQ2,subQ0])],"isStart":false})})}),makeQuery(id+"F8.opExtrude","SWEPT_FACE",FACE,{"disambiguationData":[OSD([sQuery(id+"F7.wireOp",EDGE,"E67")])]})]});}
            var Q5;
            Q5=makeQuery(id+"F8.boolean.opBoolean","INTERSECT",EDGE,{"disambiguationData":[OD(0.0)],"derivedFrom":[makeQuery(id+"F5.opExtrude","SWEPT_FACE",FACE,{"disambiguationData":[OSD([sQuery(id+"F4.wireOp",EDGE,"E30")])]}),makeQuery(id+"F8.opExtrude","SWEPT_FACE",FACE,{"disambiguationData":[OSD([sQuery(id+"F7.wireOp",EDGE,"E67")])]})]});
            fillet(context, id + "F14", {"entities" : qUnion([Q0, Q1, Q2, Q3, Q4, Q5]), "radius" : 3 * mm, "tangentPropagation" : true, "allowEdgeOverflow" : false});
        }
        {
            var Q0;
            Q0=makeQuery(id+"F1.opExtrude","CAP_EDGE",EDGE,{"disambiguationData":[OSD([sQuery(id+"F0.wireOp",EDGE,"E1.bottom")])],"isStart":false});
            fillet(context, id + "F15", {"entities" : qUnion([Q0]), "radius" : 2 * mm, "tangentPropagation" : true, "allowEdgeOverflow" : false});
        }
        {
            var Q0;
            {var subQ0=sQuery(id+"F0.wireOp",EDGE,"E1.bottom");var subQ1=sQuery(id+"F0.wireOp",EDGE,"E1.top");var subQ2=sQuery(id+"F0.wireOp",EDGE,"E1.left");var subQ3=sQuery(id+"F0.wireOp",EDGE,"E1.right");var subQ4=sQuery(id+"F0.wireOp",EDGE,"E4");var subQ5=sQuery(id+"F0.wireOp",EDGE,"E5");var subQ6=sQuery(id+"F0.wireOp",EDGE,"E6");var subQ7=sQuery(id+"F0.wireOp",EDGE,"E7");var subQ8=sQuery(id+"F0.wireOp",EDGE,"E21.filletArc");var subQ9=sQuery(id+"F0.wireOp",EDGE,"E22.filletArc");var subQ10=sQuery(id+"F0.wireOp",EDGE,"E23.filletArc");var subQ11=sQuery(id+"F0.wireOp",EDGE,"E24.filletArc");Q0=makeQuery(id+"F2.boolean.opBoolean","SPLIT",FACE,{"disambiguationData":[TD([makeQuery(id+"F1.opExtrude","SWEPT_FACE",FACE,{"disambiguationData":[OSD([subQ0])]})])],"derivedFrom":makeQuery(id+"F1.opExtrude","CAP_FACE",FACE,{"disambiguationData":[OSD([subQ0,subQ1,subQ2,subQ3,subQ4,subQ5,subQ6,subQ7,subQ8,subQ9,subQ10,subQ11])],"isStart":true})});}
            var sketch = newSketch(context, id + "F16", { "sketchPlane" : qUnion([Q0])});
            skLineSegment(sketch, "E79", {"start": v(94.05, 208.38) * mm, "end": v(94.05, 238.38) * mm, "construction": true});
            skCircle(sketch, "E80", {"center": v(94.05, 238.38) * mm, "radius": 6 * mm});
            skLineSegment(sketch, "E81", {"start": v(61.05, 208.38) * mm, "end": v(79.05, 226.38) * mm});
            skLineSegment(sketch, "E82", {"start": v(79.05, 226.38) * mm, "end": v(79.05, 238.38) * mm});
            skLineSegment(sketch, "E83", {"start": v(127.05, 208.38) * mm, "end": v(109.05, 226.38) * mm});
            skLineSegment(sketch, "E84", {"start": v(109.05, 226.38) * mm, "end": v(109.05, 238.38) * mm});
            skArc(sketch, "E85", {"start": v(109.05, 238.38) * mm, "mid": v(94.05, 253.38) * mm, "end": v(79.05, 238.38) * mm});
            skLineSegment(sketch, "E86", {"start": v(14.05, 118.38) * mm, "end": v(174.05, 118.38) * mm, "construction": true});
            skLineSegment(sketch, "E87.MirrorCS", {"start": v(127.05, 28.38) * mm, "end": v(109.05, 10.38) * mm});
            skLineSegment(sketch, "E88.MirrorCS", {"start": v(61.05, 28.38) * mm, "end": v(79.05, 10.38) * mm});
            skLineSegment(sketch, "E89.MirrorCS", {"start": v(109.05, 10.38) * mm, "end": v(109.05, -1.62) * mm});
            skLineSegment(sketch, "E90.MirrorCS", {"start": v(79.05, 10.38) * mm, "end": v(79.05, -1.62) * mm});
            skArc(sketch, "E91.MirrorCS", {"start": v(109.05, -1.62) * mm, "mid": v(94.05, -16.62) * mm, "end": v(79.05, -1.62) * mm});
            skCircle(sketch, "E92.MirrorC", {"center": v(94.05, -1.62) * mm, "radius": 6 * mm});
            skSolve(sketch);
        }
        {
            var Q0;
            Q0=makeQuery(id+"F16.imprint","IMPRINT",FACE,{"disambiguationData":[TD([[makeQuery(id+"F16.imprint","IMPRINT",EDGE,{"derivedFrom":makeQuery(id+"F1.opExtrude","CAP_EDGE",EDGE,{"disambiguationData":[OSD([sQuery(id+"F0.wireOp",EDGE,"E1.left")])],"isStart":true})}),-1.0]])]});
            var Q1;
            Q1=makeQuery(id+"F16.imprint","IMPRINT",FACE,{"disambiguationData":[TD([[makeQuery(id+"F16.imprint","IMPRINT",EDGE,{"derivedFrom":sQuery(id+"F16.wireOp",EDGE,"E80")}),-1.0]])]});
            var Q2;
            {var subQ2=sQuery(id+"F16.wireOp",EDGE,"E87.MirrorCS");Q2=makeQuery(id+"F16.imprint","IMPRINT",FACE,{"disambiguationData":[TD([[makeQuery(id+"F16.imprint","IMPRINT",EDGE,{"derivedFrom":subQ2}),-1.0]])]});}
            var Q3;
            Q3=makeQuery(id+"F2.opExtrude","CAP_FACE",FACE,{"disambiguationData":[OSD([sQuery(id+"F0.wireOp",EDGE,"E12"),sQuery(id+"F0.wireOp",EDGE,"E13"),sQuery(id+"F0.wireOp",EDGE,"E14"),sQuery(id+"F0.wireOp",EDGE,"E15"),sQuery(id+"F0.wireOp",EDGE,"E17.filletArc"),sQuery(id+"F0.wireOp",EDGE,"E18.filletArc"),sQuery(id+"F0.wireOp",EDGE,"E19.filletArc"),sQuery(id+"F0.wireOp",EDGE,"E20.filletArc"),sQuery(id+"F0.wireOp",EDGE,"E25.0"),sQuery(id+"F0.wireOp",EDGE,"E25.1"),sQuery(id+"F0.wireOp",EDGE,"E25.2"),sQuery(id+"F0.wireOp",EDGE,"E25.3"),sQuery(id+"F0.wireOp",EDGE,"E25.4"),sQuery(id+"F0.wireOp",EDGE,"E25.5"),sQuery(id+"F0.wireOp",EDGE,"E25.6"),sQuery(id+"F0.wireOp",EDGE,"E25.7")])],"isStart":false});
            extrude(context, id + "F17", {"entities" : qUnion([Q0, Q1, Q2]), "operationType" : NewBodyOperationType.ADD, "endBound" : BoundingType.UP_TO_SURFACE, "endBoundEntityFace" : qUnion([Q3]), "depth" : 25 * mm});
        }
    });
